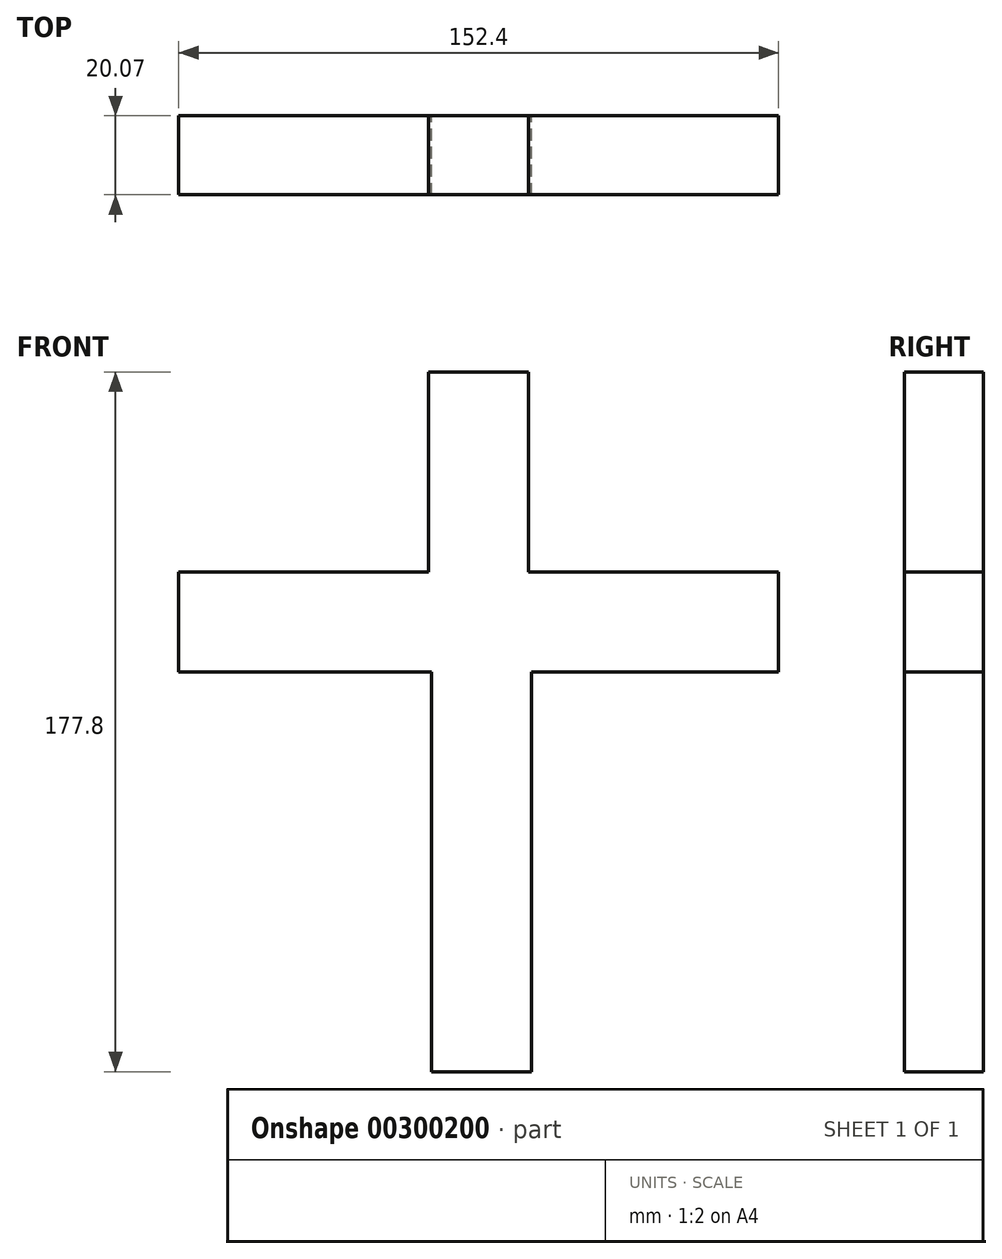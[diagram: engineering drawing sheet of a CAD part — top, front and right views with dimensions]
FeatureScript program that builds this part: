
annotation { "Feature Type Name" : "Feature", "Feature Type Description" : "" }
export const myFeature = defineFeature(function(context is Context, id is Id, definition is map)
    precondition{}
    {
        {
            var Q0;
            Q0=qCreatedBy(makeId("Front.planeOp"),FACE);
            var sketch = newSketch(context, id + "F0", { "sketchPlane" : qUnion([Q0])});
            skLineSegment(sketch, "E0", {"start": v(-9.59, 109.56) * mm, "end": v(15.81, 109.56) * mm});
            skLineSegment(sketch, "E1", {"start": v(15.81, 109.56) * mm, "end": v(15.81, 58.76) * mm});
            skLineSegment(sketch, "E2", {"start": v(15.81, 58.76) * mm, "end": v(79.31, 58.76) * mm});
            skLineSegment(sketch, "E3", {"start": v(79.31, 58.76) * mm, "end": v(79.31, 33.36) * mm});
            skLineSegment(sketch, "E4", {"start": v(79.31, 33.36) * mm, "end": v(16.5, 33.36) * mm});
            skLineSegment(sketch, "E5", {"start": v(16.5, 33.36) * mm, "end": v(16.5, -68.24) * mm});
            skLineSegment(sketch, "E6", {"start": v(16.5, -68.24) * mm, "end": v(-8.9, -68.24) * mm});
            skLineSegment(sketch, "E7", {"start": v(-8.9, -68.24) * mm, "end": v(-8.9, 33.36) * mm});
            skLineSegment(sketch, "E8", {"start": v(-8.9, 33.36) * mm, "end": v(-73.09, 33.36) * mm});
            skLineSegment(sketch, "E9", {"start": v(-73.09, 33.36) * mm, "end": v(-73.09, 58.76) * mm});
            skLineSegment(sketch, "E10", {"start": v(-73.09, 58.76) * mm, "end": v(-9.59, 58.76) * mm});
            skLineSegment(sketch, "E11", {"start": v(-9.59, 58.76) * mm, "end": v(-9.59, 109.56) * mm});
            skSolve(sketch);
        }
        {
            var Q0;
            Q0=makeQuery(id+"F0.imprint","IMPRINT",FACE,{"disambiguationData":[TD([[makeQuery(id+"F0.imprint","IMPRINT",EDGE,{"derivedFrom":sQuery(id+"F0.wireOp",EDGE,"E0")}),-1.0]])]});
            extrude(context, id + "F1", {"entities" : qUnion([Q0]), "depth" : 20.07 * mm});
        }
    });
